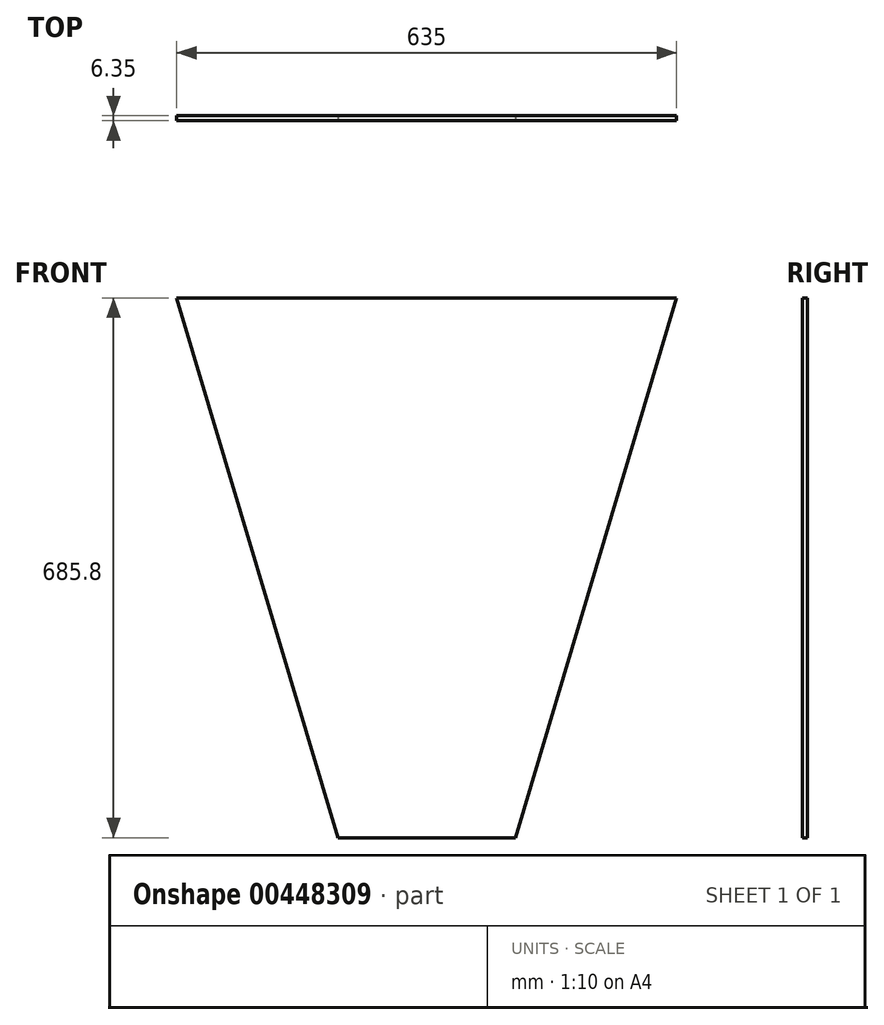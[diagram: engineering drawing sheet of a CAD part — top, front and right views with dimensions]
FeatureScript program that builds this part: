
annotation { "Feature Type Name" : "Feature", "Feature Type Description" : "" }
export const myFeature = defineFeature(function(context is Context, id is Id, definition is map)
    precondition{}
    {
        {
            var Q0;
            Q0=qCreatedBy(makeId("Front.planeOp"),FACE);
            var sketch = newSketch(context, id + "F0", { "sketchPlane" : qUnion([Q0])});
            skLineSegment(sketch, "E0", {"start": v(0, 337.06) * mm, "end": v(0, -348.74) * mm, "construction": true});
            skLineSegment(sketch, "E1", {"start": v(0, 337.06) * mm, "end": v(317.5, 337.06) * mm});
            skLineSegment(sketch, "E2", {"start": v(0, 337.06) * mm, "end": v(-317.5, 337.06) * mm});
            skPoint(sketch, "E3", {"position": v(0, -215.4) * mm});
            skLineSegment(sketch, "E4", {"start": v(0, -215.4) * mm, "end": v(152.4, -215.4) * mm, "construction": true});
            skLineSegment(sketch, "E5", {"start": v(0, -215.4) * mm, "end": v(-152.4, -215.4) * mm, "construction": true});
            skLineSegment(sketch, "E6", {"start": v(0, -348.74) * mm, "end": v(112.55, -348.74) * mm, "construction": true});
            skLineSegment(sketch, "E7", {"start": v(317.5, 337.06) * mm, "end": v(112.55, -348.74) * mm});
            skLineSegment(sketch, "E8", {"start": v(0, -348.74) * mm, "end": v(-112.55, -348.74) * mm, "construction": true});
            skLineSegment(sketch, "E9", {"start": v(-317.5, 337.06) * mm, "end": v(-112.55, -348.74) * mm});
            skLineSegment(sketch, "E10", {"start": v(-112.55, -348.74) * mm, "end": v(0, -348.74) * mm});
            skLineSegment(sketch, "E11", {"start": v(0, -348.74) * mm, "end": v(112.55, -348.74) * mm});
            skSolve(sketch);
        }
        {
            var Q0;
            Q0 = qSketchRegion(id + "F0", true);
            extrude(context, id + "F1", {"entities" : qUnion([Q0]), "oppositeDirection" : true, "depth" : 6.35 * mm});
        }
    });
